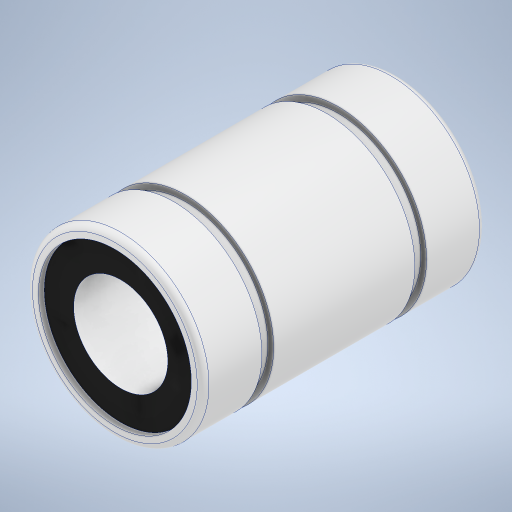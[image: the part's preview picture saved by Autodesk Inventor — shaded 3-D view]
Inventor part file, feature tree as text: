
AUTODESK INVENTOR PART (.ipt)
format: ipt  version: 2023 (Build 270158000, 158)  size: 314,880 bytes
history: native  units: mm
features: extrude x3, sketch x3, fillet x1, revolve x1, projected_geometry x1
ambient origin geometry x8: Origin, YZ Plane, XZ Plane, XY Plane, X Axis, Y Axis, Z Axis, Center Point
bodies: Solid1 (feature_tree)
feature tree (9):
  extrude  "Extrusion1"  Depth=24.0mm
  fillet  "Fillet1"  Radius=15.0mm
  revolve  "Revolution1"  [1 undecoded]
  sketch  "Sketch3"  dims[d6=1.0mm d7=0.5mm d8=90.0deg d9=1.0mm d10=0.5mm d11=0.0mm d12=0.5mm d13=0.0mm]
  extrude  "Extrusion2"  Depth=0.5mm
  extrude  "Extrusion3"  TaperAngle=90.0deg  [1 undecoded]
  sketch  "Sketch1"  dims[d0=24.0mm d1=0.0mm d2=8.0mm d3=15.0mm]
  sketch  "Sketch2"  dims[d4=0.5mm d5=5.0mm]
  projected_geometry  "Project Cut Edges1"
note: 2 required parameter values undecoded (feature->parameter linkage not recoverable at this tier; creation-order binding heuristic only, values carry confidence <= 0.55)